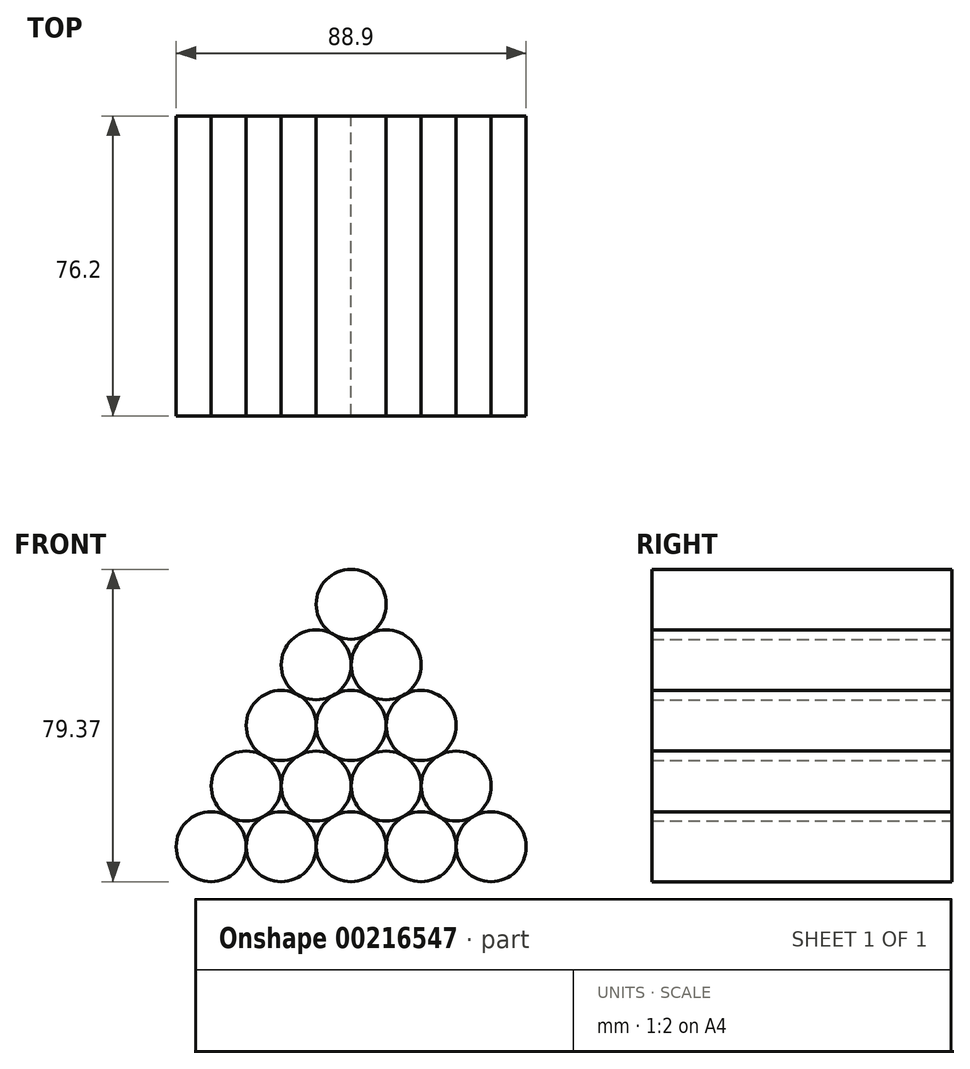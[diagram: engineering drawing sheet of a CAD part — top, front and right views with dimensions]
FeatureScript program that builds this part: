
annotation { "Feature Type Name" : "Feature", "Feature Type Description" : "" }
export const myFeature = defineFeature(function(context is Context, id is Id, definition is map)
    precondition{}
    {
        {
            var Q0;
            Q0=qCreatedBy(makeId("Front.planeOp"),FACE);
            var sketch = newSketch(context, id + "F0", { "sketchPlane" : qUnion([Q0])});
            skCircle(sketch, "E0", {"center": v(-26.67, 0) * mm, "radius": 8.9 * mm});
            skCircle(sketch, "E1", {"center": v(-8.9, 0) * mm, "radius": 8.9 * mm});
            skCircle(sketch, "E2", {"center": v(8.9, 0) * mm, "radius": 8.9 * mm});
            skCircle(sketch, "E3", {"center": v(26.67, 0) * mm, "radius": 8.9 * mm});
            skCircle(sketch, "E4", {"center": v(-17.78, 15.4) * mm, "radius": 8.9 * mm});
            skCircle(sketch, "E5", {"center": v(0, 15.4) * mm, "radius": 8.9 * mm});
            skCircle(sketch, "E6", {"center": v(17.78, 15.4) * mm, "radius": 8.9 * mm});
            skCircle(sketch, "E7", {"center": v(-35.56, -15.4) * mm, "radius": 8.9 * mm});
            skCircle(sketch, "E8", {"center": v(-17.78, -15.4) * mm, "radius": 8.9 * mm});
            skCircle(sketch, "E9", {"center": v(0, -15.4) * mm, "radius": 8.9 * mm});
            skCircle(sketch, "E10", {"center": v(17.78, -15.4) * mm, "radius": 8.9 * mm});
            skCircle(sketch, "E11", {"center": v(35.56, -15.4) * mm, "radius": 8.9 * mm});
            skCircle(sketch, "E12", {"center": v(-8.89, 30.8) * mm, "radius": 8.9 * mm});
            skCircle(sketch, "E13", {"center": v(8.9, 30.8) * mm, "radius": 8.9 * mm});
            skCircle(sketch, "E14", {"center": v(0, 46.2) * mm, "radius": 8.9 * mm});
            skCircle(sketch, "E15", {"center": v(-70.9, -77.12) * mm, "radius": 8.9 * mm});
            skCircle(sketch, "E16", {"center": v(-53.11, -77.12) * mm, "radius": 8.9 * mm});
            skCircle(sketch, "E17", {"center": v(-35.34, -76.86) * mm, "radius": 8.9 * mm});
            skCircle(sketch, "E18", {"center": v(-17.56, -76.86) * mm, "radius": 8.9 * mm});
            skCircle(sketch, "E19", {"center": v(-62.23, -61.6) * mm, "radius": 8.9 * mm});
            skCircle(sketch, "E20", {"center": v(-44.45, -61.6) * mm, "radius": 8.9 * mm});
            skCircle(sketch, "E21", {"center": v(-26.67, -61.6) * mm, "radius": 8.9 * mm});
            skCircle(sketch, "E22", {"center": v(-79.78, -92.47) * mm, "radius": 8.9 * mm});
            skCircle(sketch, "E23", {"center": v(-62, -92.52) * mm, "radius": 8.9 * mm});
            skCircle(sketch, "E24", {"center": v(-44.23, -92.21) * mm, "radius": 8.9 * mm});
            skCircle(sketch, "E25", {"center": v(-26.45, -92.26) * mm, "radius": 8.9 * mm});
            skCircle(sketch, "E26", {"center": v(-8.67, -92.26) * mm, "radius": 8.9 * mm});
            skCircle(sketch, "E27", {"center": v(-53.34, -46.2) * mm, "radius": 8.9 * mm});
            skCircle(sketch, "E28", {"center": v(-35.56, -46.2) * mm, "radius": 8.9 * mm});
            skCircle(sketch, "E29", {"center": v(-44.45, -30.8) * mm, "radius": 8.9 * mm});
            skCircle(sketch, "E30", {"center": v(18, -76.86) * mm, "radius": 8.9 * mm});
            skCircle(sketch, "E31", {"center": v(35.78, -76.86) * mm, "radius": 8.9 * mm});
            skCircle(sketch, "E32", {"center": v(53.56, -76.86) * mm, "radius": 8.9 * mm});
            skCircle(sketch, "E33", {"center": v(71.34, -76.86) * mm, "radius": 8.9 * mm});
            skCircle(sketch, "E34", {"center": v(26.9, -61.46) * mm, "radius": 8.9 * mm});
            skCircle(sketch, "E35", {"center": v(44.67, -61.46) * mm, "radius": 8.9 * mm});
            skCircle(sketch, "E36", {"center": v(62.45, -61.46) * mm, "radius": 8.9 * mm});
            skCircle(sketch, "E37", {"center": v(9.11, -92.26) * mm, "radius": 8.9 * mm});
            skCircle(sketch, "E38", {"center": v(26.9, -92.26) * mm, "radius": 8.9 * mm});
            skCircle(sketch, "E39", {"center": v(44.67, -92.1) * mm, "radius": 8.9 * mm});
            skCircle(sketch, "E40", {"center": v(62.45, -92.26) * mm, "radius": 8.9 * mm});
            skCircle(sketch, "E41", {"center": v(80.23, -92.26) * mm, "radius": 8.9 * mm});
            skCircle(sketch, "E42", {"center": v(35.78, -46.06) * mm, "radius": 8.9 * mm});
            skCircle(sketch, "E43", {"center": v(53.56, -46.06) * mm, "radius": 8.9 * mm});
            skCircle(sketch, "E44", {"center": v(44.67, -30.66) * mm, "radius": 8.9 * mm});
            skCircle(sketch, "E45", {"center": v(-26.67, -30.8) * mm, "radius": 8.9 * mm});
            skCircle(sketch, "E46", {"center": v(-8.89, -30.8) * mm, "radius": 8.9 * mm});
            skCircle(sketch, "E47", {"center": v(8.9, -30.8) * mm, "radius": 8.9 * mm});
            skCircle(sketch, "E48", {"center": v(26.67, -30.8) * mm, "radius": 8.9 * mm});
            skCircle(sketch, "E49", {"center": v(-17.78, -46.2) * mm, "radius": 8.9 * mm});
            skCircle(sketch, "E50", {"center": v(0, -46.2) * mm, "radius": 8.9 * mm});
            skCircle(sketch, "E51", {"center": v(17.78, -46.2) * mm, "radius": 8.9 * mm});
            skCircle(sketch, "E52", {"center": v(-8.89, -61.6) * mm, "radius": 8.9 * mm});
            skCircle(sketch, "E53", {"center": v(8.9, -61.6) * mm, "radius": 8.9 * mm});
            skCircle(sketch, "E54", {"center": v(-1.36, -77.9) * mm, "radius": 8.9 * mm});
            skSolve(sketch);
        }
        {
            var Q0;
            {var subQ0=sQuery(id+"F0.wireOp",EDGE,"E4");var subQ1=makeQuery(id+"F0.imprint","INTERSECT",VERTEX,{"derivedFrom":[sQuery(id+"F0.wireOp",EDGE,"E0"),subQ0]});Q0=makeQuery(id+"F0.imprint","IMPRINT",FACE,{"disambiguationData":[TD([[makeQuery(id+"F0.imprint","IMPRINT",EDGE,{"disambiguationData":[TD([[subQ1,1.0]])],"derivedFrom":subQ0}),1.0]])]});}
            var Q1;
            {var subQ0=sQuery(id+"F0.wireOp",EDGE,"E5");var subQ1=makeQuery(id+"F0.imprint","INTERSECT",VERTEX,{"derivedFrom":[sQuery(id+"F0.wireOp",EDGE,"E4"),subQ0]});Q1=makeQuery(id+"F0.imprint","IMPRINT",FACE,{"disambiguationData":[TD([[makeQuery(id+"F0.imprint","IMPRINT",EDGE,{"disambiguationData":[TD([[subQ1,1.0]])],"derivedFrom":subQ0}),1.0]])]});}
            var Q2;
            {var subQ0=sQuery(id+"F0.wireOp",EDGE,"E6");var subQ1=makeQuery(id+"F0.imprint","INTERSECT",VERTEX,{"derivedFrom":[sQuery(id+"F0.wireOp",EDGE,"E5"),subQ0]});Q2=makeQuery(id+"F0.imprint","IMPRINT",FACE,{"disambiguationData":[TD([[makeQuery(id+"F0.imprint","IMPRINT",EDGE,{"disambiguationData":[TD([[subQ1,-1.0]])],"derivedFrom":subQ0}),1.0]])]});}
            var Q3;
            {var subQ0=sQuery(id+"F0.wireOp",EDGE,"E3");var subQ1=makeQuery(id+"F0.imprint","INTERSECT",VERTEX,{"derivedFrom":[subQ0,sQuery(id+"F0.wireOp",EDGE,"E6")]});Q3=makeQuery(id+"F0.imprint","IMPRINT",FACE,{"disambiguationData":[TD([[makeQuery(id+"F0.imprint","IMPRINT",EDGE,{"disambiguationData":[TD([[subQ1,-1.0]])],"derivedFrom":subQ0}),1.0]])]});}
            var Q4;
            {var subQ0=sQuery(id+"F0.wireOp",EDGE,"E2");var subQ4=makeQuery(id+"F0.imprint","INTERSECT",VERTEX,{"derivedFrom":[subQ0,sQuery(id+"F0.wireOp",EDGE,"E6")]});Q4=makeQuery(id+"F0.imprint","IMPRINT",FACE,{"disambiguationData":[TD([[makeQuery(id+"F0.imprint","IMPRINT",EDGE,{"disambiguationData":[TD([[subQ4,1.0]])],"derivedFrom":subQ0}),1.0]])]});}
            var Q5;
            {var subQ0=sQuery(id+"F0.wireOp",EDGE,"E1");var subQ4=makeQuery(id+"F0.imprint","INTERSECT",VERTEX,{"derivedFrom":[subQ0,sQuery(id+"F0.wireOp",EDGE,"E5")]});Q5=makeQuery(id+"F0.imprint","IMPRINT",FACE,{"disambiguationData":[TD([[makeQuery(id+"F0.imprint","IMPRINT",EDGE,{"disambiguationData":[TD([[subQ4,1.0]])],"derivedFrom":subQ0}),1.0]])]});}
            var Q6;
            {var subQ0=sQuery(id+"F0.wireOp",EDGE,"E0");var subQ1=makeQuery(id+"F0.imprint","INTERSECT",VERTEX,{"derivedFrom":[subQ0,sQuery(id+"F0.wireOp",EDGE,"E4")]});Q6=makeQuery(id+"F0.imprint","IMPRINT",FACE,{"disambiguationData":[TD([[makeQuery(id+"F0.imprint","IMPRINT",EDGE,{"disambiguationData":[TD([[subQ1,1.0]])],"derivedFrom":subQ0}),1.0]])]});}
            var Q7;
            {var subQ0=sQuery(id+"F0.wireOp",EDGE,"E7");var subQ1=makeQuery(id+"F0.imprint","INTERSECT",VERTEX,{"derivedFrom":[sQuery(id+"F0.wireOp",EDGE,"E0"),subQ0]});Q7=makeQuery(id+"F0.imprint","IMPRINT",FACE,{"disambiguationData":[TD([[makeQuery(id+"F0.imprint","IMPRINT",EDGE,{"disambiguationData":[TD([[subQ1,1.0]])],"derivedFrom":subQ0}),1.0]])]});}
            var Q8;
            {var subQ0=sQuery(id+"F0.wireOp",EDGE,"E8");var subQ4=makeQuery(id+"F0.imprint","INTERSECT",VERTEX,{"derivedFrom":[sQuery(id+"F0.wireOp",EDGE,"E1"),subQ0]});Q8=makeQuery(id+"F0.imprint","IMPRINT",FACE,{"disambiguationData":[TD([[makeQuery(id+"F0.imprint","IMPRINT",EDGE,{"disambiguationData":[TD([[subQ4,1.0]])],"derivedFrom":subQ0}),1.0]])]});}
            var Q9;
            {var subQ0=sQuery(id+"F0.wireOp",EDGE,"E9");var subQ4=makeQuery(id+"F0.imprint","INTERSECT",VERTEX,{"derivedFrom":[sQuery(id+"F0.wireOp",EDGE,"E2"),subQ0]});Q9=makeQuery(id+"F0.imprint","IMPRINT",FACE,{"disambiguationData":[TD([[makeQuery(id+"F0.imprint","IMPRINT",EDGE,{"disambiguationData":[TD([[subQ4,1.0]])],"derivedFrom":subQ0}),1.0]])]});}
            var Q10;
            {var subQ0=sQuery(id+"F0.wireOp",EDGE,"E10");var subQ4=makeQuery(id+"F0.imprint","INTERSECT",VERTEX,{"derivedFrom":[sQuery(id+"F0.wireOp",EDGE,"E3"),subQ0]});Q10=makeQuery(id+"F0.imprint","IMPRINT",FACE,{"disambiguationData":[TD([[makeQuery(id+"F0.imprint","IMPRINT",EDGE,{"disambiguationData":[TD([[subQ4,1.0]])],"derivedFrom":subQ0}),1.0]])]});}
            var Q11;
            {var subQ0=sQuery(id+"F0.wireOp",EDGE,"E11");var subQ1=makeQuery(id+"F0.imprint","INTERSECT",VERTEX,{"derivedFrom":[sQuery(id+"F0.wireOp",EDGE,"E3"),subQ0]});Q11=makeQuery(id+"F0.imprint","IMPRINT",FACE,{"disambiguationData":[TD([[makeQuery(id+"F0.imprint","IMPRINT",EDGE,{"disambiguationData":[TD([[subQ1,-1.0]])],"derivedFrom":subQ0}),1.0]])]});}
            var Q12;
            Q12=makeQuery(id+"F0.imprint","IMPRINT",FACE,{"disambiguationData":[TD([[makeQuery(id+"F0.imprint","IMPRINT",EDGE,{"derivedFrom":sQuery(id+"F0.wireOp",EDGE,"7U8sLhQw-9m7X-TW6Q-3LMa-rkqMw9JBz2WS.top")}),1.0]])]});
            var Q13;
            {var subQ0=sQuery(id+"F0.wireOp",EDGE,"E12");var subQ1=makeQuery(id+"F0.imprint","INTERSECT",VERTEX,{"derivedFrom":[subQ0,sQuery(id+"F0.wireOp",EDGE,"E14")]});Q13=makeQuery(id+"F0.imprint","IMPRINT",FACE,{"disambiguationData":[TD([[makeQuery(id+"F0.imprint","IMPRINT",EDGE,{"disambiguationData":[TD([[subQ1,1.0]])],"derivedFrom":subQ0}),1.0]])]});}
            var Q14;
            {var subQ0=sQuery(id+"F0.wireOp",EDGE,"E13");var subQ1=makeQuery(id+"F0.imprint","INTERSECT",VERTEX,{"derivedFrom":[subQ0,sQuery(id+"F0.wireOp",EDGE,"E14")]});Q14=makeQuery(id+"F0.imprint","IMPRINT",FACE,{"disambiguationData":[TD([[makeQuery(id+"F0.imprint","IMPRINT",EDGE,{"disambiguationData":[TD([[subQ1,-1.0]])],"derivedFrom":subQ0}),1.0]])]});}
            var Q15;
            {var subQ0=sQuery(id+"F0.wireOp",EDGE,"E14");var subQ1=makeQuery(id+"F0.imprint","INTERSECT",VERTEX,{"derivedFrom":[sQuery(id+"F0.wireOp",EDGE,"E12"),subQ0]});Q15=makeQuery(id+"F0.imprint","IMPRINT",FACE,{"disambiguationData":[TD([[makeQuery(id+"F0.imprint","IMPRINT",EDGE,{"disambiguationData":[TD([[subQ1,-1.0]])],"derivedFrom":subQ0}),1.0]])]});}
            var Q16;
            Q16=sQuery(id+"F0.wireOp",EDGE,"E5");
            var Q17;
            Q17=sQuery(id+"F0.wireOp",EDGE,"E6");
            var Q18;
            Q18=sQuery(id+"F0.wireOp",EDGE,"7U8sLhQw-9m7X-TW6Q-3LMa-rkqMw9JBz2WS.bottom");
            var Q19;
            Q19=sQuery(id+"F0.wireOp",EDGE,"E1");
            var Q20;
            Q20=sQuery(id+"F0.wireOp",EDGE,"E3");
            var Q21;
            Q21=sQuery(id+"F0.wireOp",EDGE,"E4");
            var Q22;
            Q22=sQuery(id+"F0.wireOp",EDGE,"E11");
            var Q23;
            Q23=sQuery(id+"F0.wireOp",EDGE,"E8");
            var Q24;
            Q24=sQuery(id+"F0.wireOp",EDGE,"E2");
            var Q25;
            Q25=sQuery(id+"F0.wireOp",EDGE,"7U8sLhQw-9m7X-TW6Q-3LMa-rkqMw9JBz2WS.top");
            var Q26;
            Q26=sQuery(id+"F0.wireOp",EDGE,"E0");
            var Q27;
            Q27=sQuery(id+"F0.wireOp",EDGE,"E9");
            var Q28;
            Q28=sQuery(id+"F0.wireOp",EDGE,"E10");
            var Q29;
            Q29=sQuery(id+"F0.wireOp",EDGE,"E7");
            var Q30;
            Q30=sQuery(id+"F0.wireOp",EDGE,"7U8sLhQw-9m7X-TW6Q-3LMa-rkqMw9JBz2WS.left");
            var Q31;
            Q31=sQuery(id+"F0.wireOp",EDGE,"7U8sLhQw-9m7X-TW6Q-3LMa-rkqMw9JBz2WS.right");
            extrude(context, id + "F1", {"entities" : qUnion([Q0, Q1, Q2, Q3, Q4, Q5, Q6, Q7, Q8, Q9, Q10, Q11, Q12, Q13, Q14, Q15]), "surfaceEntities" : qUnion([Q16, Q17, Q18, Q19, Q20, Q21, Q22, Q23, Q24, Q25, Q26, Q27, Q28, Q29, Q30, Q31]), "depth" : 76.2 * mm});
        }
    });
